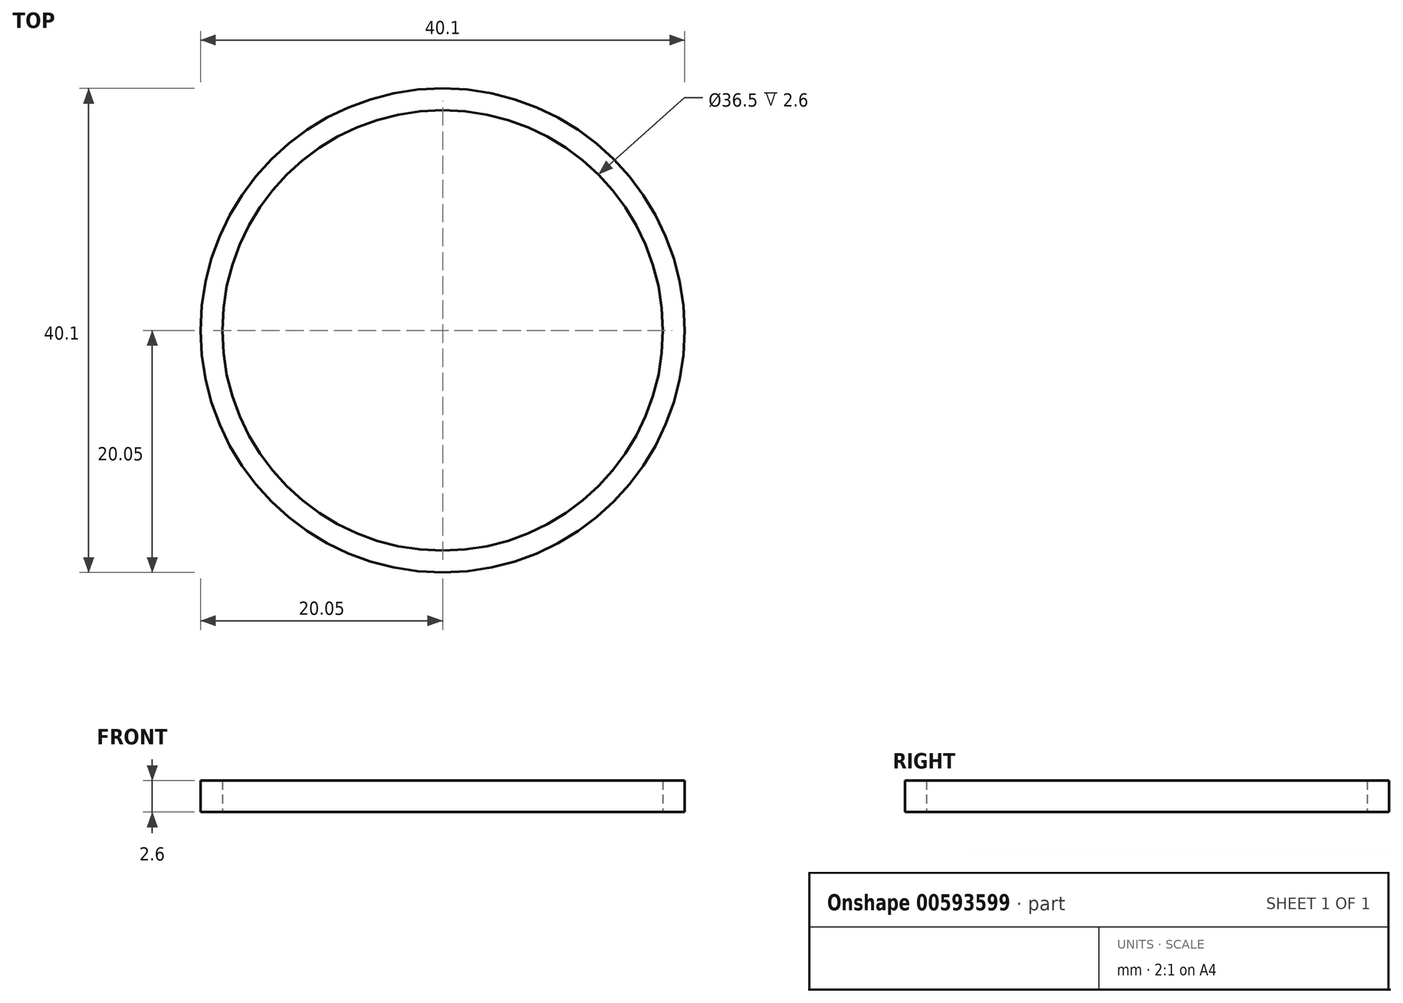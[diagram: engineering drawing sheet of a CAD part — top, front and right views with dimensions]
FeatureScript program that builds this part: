
annotation { "Feature Type Name" : "Feature", "Feature Type Description" : "" }
export const myFeature = defineFeature(function(context is Context, id is Id, definition is map)
    precondition{}
    {
        {
            var Q0;
            Q0=qCreatedBy(makeId("Top.planeOp"),FACE);
            var sketch = newSketch(context, id + "F0", { "sketchPlane" : qUnion([Q0])});
            skCircle(sketch, "E0", {"center": v(0, 0) * mm, "radius": 18.25 * mm});
            skCircle(sketch, "E1.0", {"center": v(0, 0) * mm, "radius": 20.05 * mm});
            skSolve(sketch);
        }
        {
            var Q0;
            Q0 = qSketchRegion(id + "F0", true);
            extrude(context, id + "F1", {"entities" : qUnion([Q0]), "depth" : 2.6 * mm, "offsetDistance" : 25 * mm});
        }
    });
